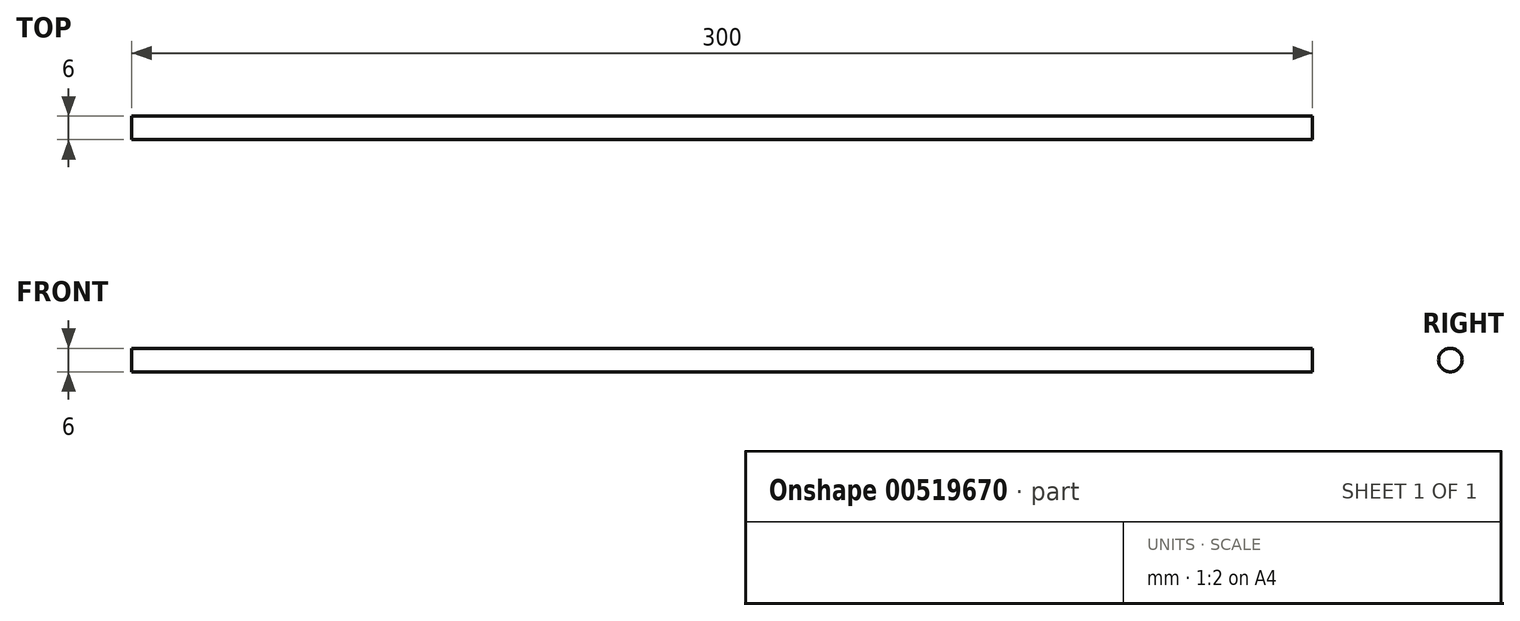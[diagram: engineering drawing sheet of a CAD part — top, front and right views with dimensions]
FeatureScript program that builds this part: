
annotation { "Feature Type Name" : "Feature", "Feature Type Description" : "" }
export const myFeature = defineFeature(function(context is Context, id is Id, definition is map)
    precondition{}
    {
        {
            var Q0;
            Q0=qCreatedBy(makeId("Right.planeOp"),FACE);
            var sketch = newSketch(context, id + "F0", { "sketchPlane" : qUnion([Q0])});
            skCircle(sketch, "E0", {"center": v(0, 0) * mm, "radius": 3 * mm});
            skSolve(sketch);
        }
        {
            var Q0;
            Q0=makeQuery(id+"F0.imprint","IMPRINT",FACE,{"disambiguationData":[TD([[makeQuery(id+"F0.imprint","IMPRINT",EDGE,{"derivedFrom":sQuery(id+"F0.wireOp",EDGE,"E0")}),1.0]])]});
            extrude(context, id + "F1", {"entities" : qUnion([Q0]), "depth" : 300 * mm, "offsetDistance" : 25 * mm});
        }
    });
